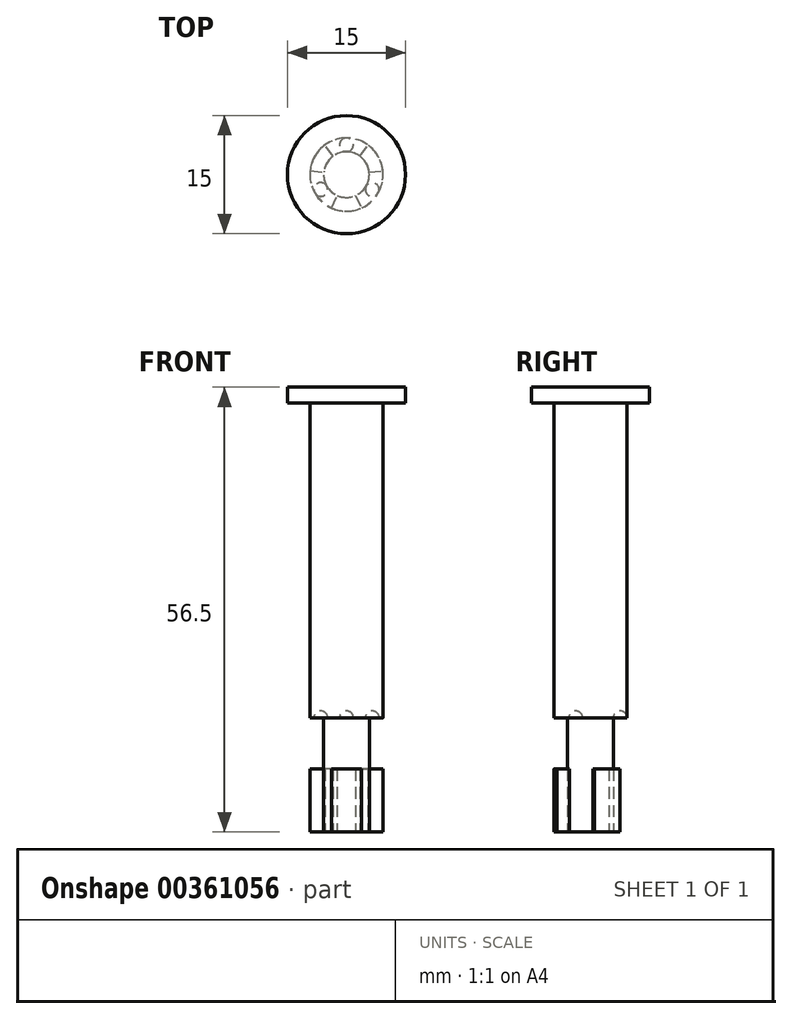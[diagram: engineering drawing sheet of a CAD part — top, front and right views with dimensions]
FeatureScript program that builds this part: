
annotation { "Feature Type Name" : "Feature", "Feature Type Description" : "" }
export const myFeature = defineFeature(function(context is Context, id is Id, definition is map)
    precondition{}
    {
        {
            var Q0;
            Q0=qCreatedBy(makeId("Top.planeOp"),FACE);
            var sketch = newSketch(context, id + "F0", { "sketchPlane" : qUnion([Q0])});
            skArc(sketch, "E0", {"start": v(-2.73, 3.76) * mm, "mid": v(-4.03, 2.32) * mm, "end": v(-4.62, 0.49) * mm});
            skCircle(sketch, "E1.0", {"center": v(0, 0) * mm, "radius": 2.9 * mm});
            skLineSegment(sketch, "E2", {"start": v(1.7, 2.35) * mm, "end": v(2.73, 3.76) * mm});
            skLineSegment(sketch, "E3", {"start": v(-1.7, 2.35) * mm, "end": v(-2.73, 3.76) * mm});
            skLineSegment(sketch, "E4.1.1", {"start": v(-1.18, -2.65) * mm, "end": v(-1.9, -4.25) * mm, "construction": true});
            skLineSegment(sketch, "E4.1.2", {"start": v(-2.88, 0.3) * mm, "end": v(-4.62, 0.49) * mm, "construction": true});
            skArc(sketch, "E4.2.0", {"start": v(-2.73, 3.76) * mm, "mid": v(-4.03, 2.33) * mm, "end": v(-4.62, 0.49) * mm});
            skLineSegment(sketch, "E4.2.1", {"start": v(2.88, 0.3) * mm, "end": v(4.62, 0.49) * mm, "construction": true});
            skLineSegment(sketch, "E4.2.2", {"start": v(1.18, -2.65) * mm, "end": v(1.9, -4.25) * mm, "construction": true});
            skLineSegment(sketch, "E5", {"start": v(-1.9, -4.25) * mm, "end": v(-1.18, -2.65) * mm});
            skLineSegment(sketch, "E6", {"start": v(-4.62, 0.49) * mm, "end": v(-2.88, 0.3) * mm});
            skLineSegment(sketch, "E7", {"start": v(1.18, -2.65) * mm, "end": v(1.9, -4.25) * mm});
            skLineSegment(sketch, "E8", {"start": v(2.88, 0.3) * mm, "end": v(4.62, 0.49) * mm});
            skArc(sketch, "E9.trimOffspring", {"start": v(-1.9, -4.25) * mm, "mid": v(0, -4.65) * mm, "end": v(1.9, -4.25) * mm});
            skArc(sketch, "E10.trimOffspring", {"start": v(4.62, 0.49) * mm, "mid": v(4.03, 2.33) * mm, "end": v(2.73, 3.76) * mm});
            skArc(sketch, "E11.trimOffspring", {"start": v(4.62, 0.49) * mm, "mid": v(4.03, 2.32) * mm, "end": v(2.73, 3.76) * mm});
            skSolve(sketch);
        }
        {
            var Q0;
            {var subQ0=sQuery(id+"F0.wireOp",EDGE,"E3");Q0=makeQuery(id+"F0.imprint","IMPRINT",FACE,{"disambiguationData":[TD([[makeQuery(id+"F0.imprint","IMPRINT",EDGE,{"derivedFrom":subQ0}),1.0]])]});}
            var Q1;
            {var subQ0=sQuery(id+"F0.wireOp",EDGE,"E2");Q1=makeQuery(id+"F0.imprint","IMPRINT",FACE,{"disambiguationData":[TD([[makeQuery(id+"F0.imprint","IMPRINT",EDGE,{"derivedFrom":subQ0}),-1.0]])]});}
            var Q2;
            {var subQ0=sQuery(id+"F0.wireOp",EDGE,"E5");Q2=makeQuery(id+"F0.imprint","IMPRINT",FACE,{"disambiguationData":[TD([[makeQuery(id+"F0.imprint","IMPRINT",EDGE,{"derivedFrom":subQ0}),-1.0]])]});}
            extrude(context, id + "F1", {"entities" : qUnion([Q0, Q1, Q2]), "depth" : 8 * mm});
        }
        {
            var Q0;
            {var subQ0=sQuery(id+"F0.wireOp",EDGE,"E1.0");var subQ4=makeQuery(id+"F0.imprint","INTERSECT",VERTEX,{"derivedFrom":[subQ0,sQuery(id+"F0.wireOp",EDGE,"E2")]});Q0=makeQuery(id+"F0.imprint","IMPRINT",FACE,{"disambiguationData":[TD([[makeQuery(id+"F0.imprint","IMPRINT",EDGE,{"disambiguationData":[TD([[subQ4,1.0]])],"derivedFrom":subQ0}),1.0]])]});}
            extrude(context, id + "F2", {"entities" : qUnion([Q0]), "depth" : (8 + 6.5) * mm});
        }
        {
            var Q0;
            Q0=makeQuery(id+"F2.opExtrude","CAP_FACE",FACE,{"disambiguationData":[OSD([sQuery(id+"F0.wireOp",EDGE,"E1.0")])],"isStart":false});
            var sketch = newSketch(context, id + "F3", { "sketchPlane" : qUnion([Q0])});
            skCircle(sketch, "E12", {"center": v(0, 0) * mm, "radius": 4.65 * mm});
            skSolve(sketch);
        }
        {
            var Q0;
            Q0=makeQuery(id+"F3.imprint","IMPRINT",FACE,{"disambiguationData":[TD([[makeQuery(id+"F3.imprint","IMPRINT",EDGE,{"derivedFrom":sQuery(id+"F3.wireOp",EDGE,"E12")}),1.0]])]});
            var Q1;
            Q1=makeQuery(id+"F3.imprint","IMPRINT",FACE,{"disambiguationData":[TD([[makeQuery(id+"F3.imprint","IMPRINT",EDGE,{"derivedFrom":makeQuery(id+"F2.opExtrude","CAP_EDGE",EDGE,{"disambiguationData":[OSD([sQuery(id+"F0.wireOp",EDGE,"E1.0")])],"isStart":false})}),1.0]])]});
            extrude(context, id + "F4", {"entities" : qUnion([Q0, Q1]), "operationType" : NewBodyOperationType.ADD, "depth" : 40 * mm});
        }
        {
            var Q0;
            Q0=makeQuery(id+"F4.opExtrude","CAP_FACE",FACE,{"disambiguationData":[OSD([sQuery(id+"F3.wireOp",EDGE,"E12")])],"isStart":false});
            var sketch = newSketch(context, id + "F5", { "sketchPlane" : qUnion([Q0])});
            skCircle(sketch, "E13", {"center": v(0, 0) * mm, "radius": 7.5 * mm});
            skSolve(sketch);
        }
        {
            var Q0;
            Q0=makeQuery(id+"F5.imprint","IMPRINT",FACE,{"disambiguationData":[TD([[makeQuery(id+"F5.imprint","IMPRINT",EDGE,{"derivedFrom":sQuery(id+"F5.wireOp",EDGE,"E13")}),1.0]])]});
            var Q1;
            Q1=makeQuery(id+"F5.imprint","IMPRINT",FACE,{"disambiguationData":[TD([[makeQuery(id+"F5.imprint","IMPRINT",EDGE,{"derivedFrom":makeQuery(id+"F4.opExtrude","CAP_EDGE",EDGE,{"disambiguationData":[OSD([sQuery(id+"F3.wireOp",EDGE,"E12")])],"isStart":false})}),1.0]])]});
            extrude(context, id + "F6", {"entities" : qUnion([Q0, Q1]), "operationType" : NewBodyOperationType.ADD, "depth" : 2 * mm, "offsetDistance" : 25 * mm});
        }
        {
            var Q0;
            Q0=makeQuery(id+"F4.opExtrude","CAP_FACE",FACE,{"disambiguationData":[OSD([sQuery(id+"F3.wireOp",EDGE,"E12")])],"isStart":true});
            var sketch = newSketch(context, id + "F7", { "sketchPlane" : qUnion([Q0])});
            skLineSegment(sketch, "E14", {"start": v(0, 0) * mm, "end": v(0, -4.65) * mm, "construction": true});
            skLineSegment(sketch, "E15", {"start": v(-2.51, 1.45) * mm, "end": v(-4.03, 2.32) * mm, "construction": true});
            skLineSegment(sketch, "E16", {"start": v(2.51, 1.45) * mm, "end": v(4.03, 2.33) * mm, "construction": true});
            skCircle(sketch, "E17", {"center": v(0, 0) * mm, "radius": 3.78 * mm, "construction": true});
            skPoint(sketch, "E18", {"position": v(-3.27, 1.89) * mm});
            skPoint(sketch, "E19", {"position": v(0, -3.78) * mm});
            skPoint(sketch, "E20", {"position": v(3.27, 1.89) * mm});
            skArc(sketch, "E21", {"start": v(-4.03, 2.32) * mm, "mid": v(-3.7, 1.13) * mm, "end": v(-2.51, 1.45) * mm});
            skArc(sketch, "E22", {"start": v(4.03, 2.33) * mm, "mid": v(2.83, 2.65) * mm, "end": v(2.51, 1.45) * mm});
            skPoint(sketch, "E23", {"position": v(0, -2.9) * mm});
            skArc(sketch, "E24", {"start": v(0, -4.65) * mm, "mid": v(0.88, -3.78) * mm, "end": v(0, -2.9) * mm});
            skLineSegment(sketch, "E25", {"start": v(-4.03, 2.32) * mm, "end": v(-2.51, 1.45) * mm});
            skLineSegment(sketch, "E26", {"start": v(2.51, 1.45) * mm, "end": v(4.03, 2.33) * mm});
            skLineSegment(sketch, "E27", {"start": v(0, -2.9) * mm, "end": v(0, -4.65) * mm});
            skSolve(sketch);
        }
        {
            var Q0;
            Q0=makeQuery(id+"F7.imprint","IMPRINT",FACE,{"disambiguationData":[TD([[makeQuery(id+"F7.imprint","IMPRINT",EDGE,{"derivedFrom":sQuery(id+"F7.wireOp",EDGE,"E21")}),1.0]])]});
            var Q1;
            Q1=sQuery(id+"F7.wireOp",EDGE,"E25");
            revolve(context, id + "F8", {"operationType" : NewBodyOperationType.REMOVE, "entities" : qUnion([Q0]), "axis" : qUnion([Q1]), "revolveType" : RevolveType.FULL});
        }
        {
            var Q0;
            Q0=makeQuery(id+"F7.imprint","IMPRINT",FACE,{"disambiguationData":[TD([[makeQuery(id+"F7.imprint","IMPRINT",EDGE,{"derivedFrom":sQuery(id+"F7.wireOp",EDGE,"E22")}),1.0]])]});
            var Q1;
            Q1=sQuery(id+"F7.wireOp",EDGE,"E26");
            revolve(context, id + "F9", {"operationType" : NewBodyOperationType.REMOVE, "entities" : qUnion([Q0]), "axis" : qUnion([Q1]), "revolveType" : RevolveType.FULL, "oppositeDirection" : true});
        }
        {
            var Q0;
            Q0=makeQuery(id+"F7.imprint","IMPRINT",FACE,{"disambiguationData":[TD([[makeQuery(id+"F7.imprint","IMPRINT",EDGE,{"derivedFrom":sQuery(id+"F7.wireOp",EDGE,"E24")}),1.0]])]});
            var Q1;
            Q1=sQuery(id+"F7.wireOp",EDGE,"E27");
            revolve(context, id + "F10", {"operationType" : NewBodyOperationType.REMOVE, "entities" : qUnion([Q0]), "axis" : qUnion([Q1]), "revolveType" : RevolveType.FULL, "oppositeDirection" : true});
        }
    });
